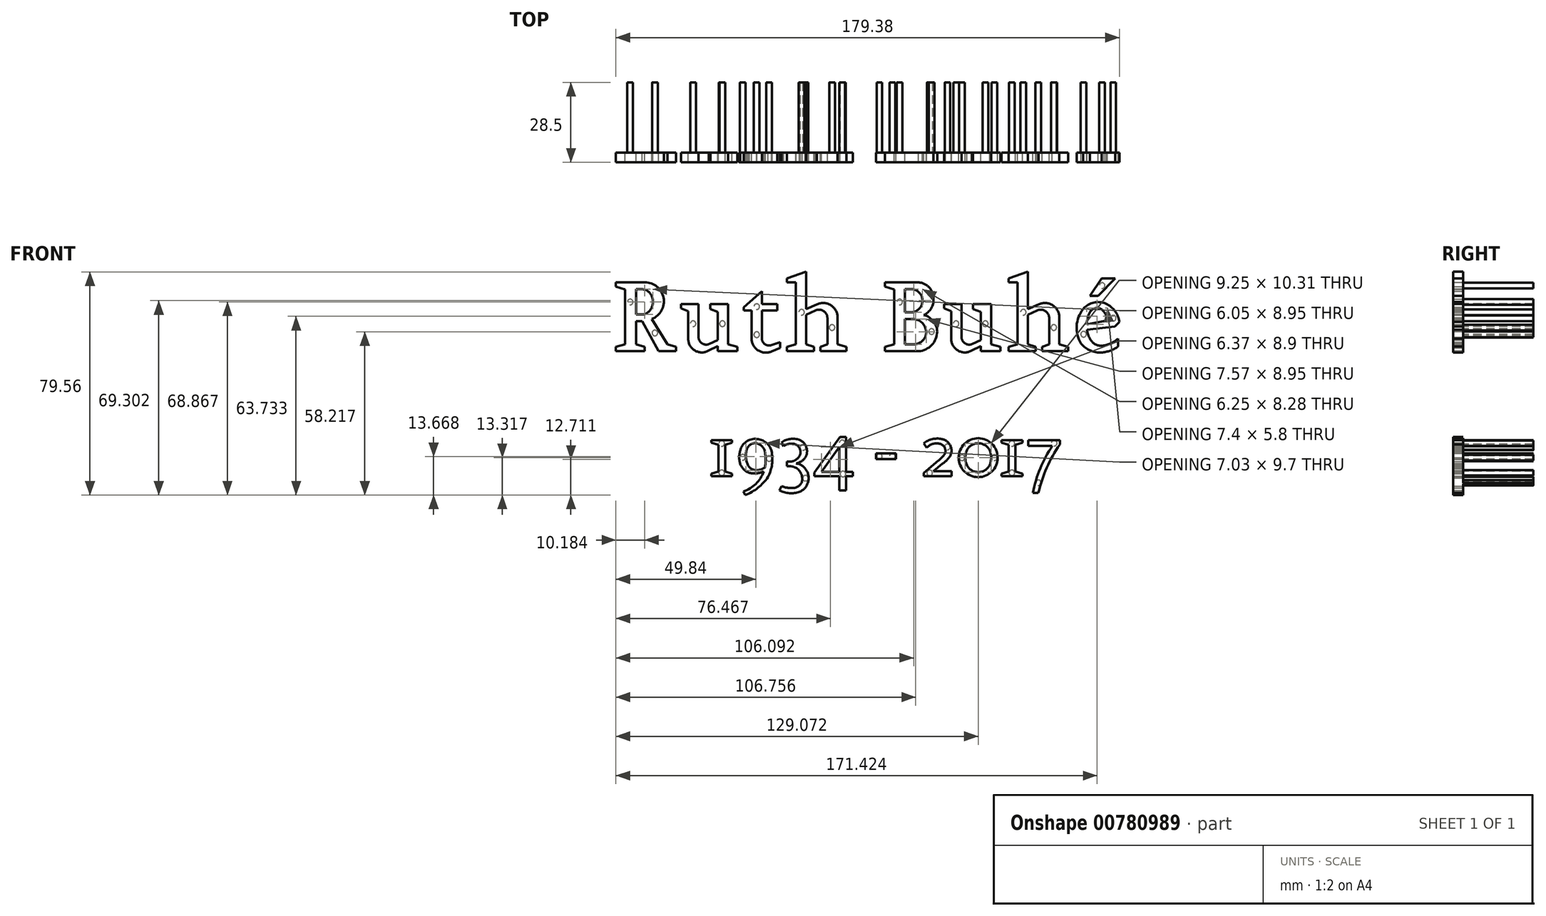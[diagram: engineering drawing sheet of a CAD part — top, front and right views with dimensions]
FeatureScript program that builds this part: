
annotation { "Feature Type Name" : "Feature", "Feature Type Description" : "" }
export const myFeature = defineFeature(function(context is Context, id is Id, definition is map)
    precondition{}
    {
        {
            var Q0;
            Q0=qCreatedBy(makeId("Front.planeOp"),FACE);
            var sketch = newSketch(context, id + "F0", { "sketchPlane" : qUnion([Q0])});
            skLineSegment(sketch, "E0", {"start": v(-78.02, 15.2) * mm, "end": v(-67.8, 15.2) * mm});
            skLineSegment(sketch, "E1", {"start": v(-67.8, 15.2) * mm, "end": v(-67.8, 16.73) * mm});
            skLineSegment(sketch, "E2", {"start": v(-67.8, 16.73) * mm, "end": v(-70.86, 17.67) * mm});
            skLineSegment(sketch, "E3", {"start": v(-70.86, 17.67) * mm, "end": v(-70.86, 25.9) * mm});
            skLineSegment(sketch, "E4", {"start": v(-70.86, 25.9) * mm, "end": v(-68.64, 25.9) * mm});
            skLineSegment(sketch, "E5", {"start": v(-68.64, 25.9) * mm, "end": v(-62.81, 15.2) * mm});
            skLineSegment(sketch, "E6", {"start": v(-62.81, 15.2) * mm, "end": v(-56.63, 15.2) * mm});
            skLineSegment(sketch, "E7", {"start": v(-56.63, 15.2) * mm, "end": v(-56.63, 16.73) * mm});
            skLineSegment(sketch, "E8", {"start": v(-56.63, 16.73) * mm, "end": v(-59.61, 17.67) * mm});
            skLineSegment(sketch, "E9", {"start": v(-59.61, 17.67) * mm, "end": v(-65.23, 26.62) * mm});
            skLineSegment(sketch, "E10", {"start": v(-78.02, 15.2) * mm, "end": v(-78.02, 16.73) * mm});
            skLineSegment(sketch, "E11", {"start": v(-78.02, 16.73) * mm, "end": v(-74.74, 17.67) * mm});
            skLineSegment(sketch, "E12", {"start": v(-74.74, 17.67) * mm, "end": v(-74.74, 37.23) * mm});
            skLineSegment(sketch, "E13", {"start": v(-74.74, 37.23) * mm, "end": v(-78.02, 38.21) * mm});
            skLineSegment(sketch, "E14", {"start": v(-78.02, 38.21) * mm, "end": v(-78.02, 39.74) * mm});
            skLineSegment(sketch, "E15", {"start": v(-78.02, 39.74) * mm, "end": v(-68.86, 39.74) * mm});
            skArc(sketch, "E16", {"start": v(-65.23, 26.62) * mm, "mid": v(-61.06, 34.23) * mm, "end": v(-67.76, 39.74) * mm});
            skArc(sketch, "E17", {"start": v(-67.74, 28.32) * mm, "mid": v(-64.81, 32.8) * mm, "end": v(-67.74, 37.27) * mm});
            skLineSegment(sketch, "E18", {"start": v(-67.74, 37.27) * mm, "end": v(-70.86, 37.27) * mm});
            skLineSegment(sketch, "E19", {"start": v(-70.86, 37.27) * mm, "end": v(-70.86, 28.32) * mm});
            skLineSegment(sketch, "E20", {"start": v(-70.86, 28.32) * mm, "end": v(-67.74, 28.32) * mm});
            skLineSegment(sketch, "E21", {"start": v(-68.86, 39.74) * mm, "end": v(-67.76, 39.74) * mm});
            skSolve(sketch);
        }
        {
            var Q0;
            Q0=makeQuery(id+"F0.imprint","IMPRINT",FACE,{"disambiguationData":[TD([[makeQuery(id+"F0.imprint","IMPRINT",EDGE,{"derivedFrom":sQuery(id+"F0.wireOp",EDGE,"E0")}),1.0]])]});
            extrude(context, id + "F1", {"entities" : qUnion([Q0]), "depth" : 3.5 * mm, "offsetDistance" : 25 * mm});
        }
        {
            var Q0;
            Q0=makeQuery(id+"F1.opExtrude","SWEPT_EDGE",EDGE,{"disambiguationData":[OSD([sQuery(id+"F0.wireOp",EDGE,"E17"),sQuery(id+"F0.wireOp",EDGE,"E18")])]});
            var Q1;
            Q1=makeQuery(id+"F1.opExtrude","SWEPT_EDGE",EDGE,{"disambiguationData":[OSD([sQuery(id+"F0.wireOp",EDGE,"E17"),sQuery(id+"F0.wireOp",EDGE,"E20")])]});
            fillet(context, id + "F2", {"entities" : qUnion([Q0, Q1]), "radius" : 3 * mm, "tangentPropagation" : true, "allowEdgeOverflow" : false});
        }
        {
            var Q0;
            Q0=qCreatedBy(makeId("Front.planeOp"),FACE);
            var sketch = newSketch(context, id + "F3", { "sketchPlane" : qUnion([Q0])});
            skLineSegment(sketch, "E22", {"start": v(-41.77, 15.2) * mm, "end": v(-34.7, 15.2) * mm});
            skLineSegment(sketch, "E23", {"start": v(-34.7, 15.2) * mm, "end": v(-34.7, 16.73) * mm});
            skLineSegment(sketch, "E24", {"start": v(-34.7, 16.73) * mm, "end": v(-38.08, 17.67) * mm});
            skLineSegment(sketch, "E25", {"start": v(-38.08, 17.67) * mm, "end": v(-38.08, 32) * mm});
            skLineSegment(sketch, "E26", {"start": v(-38.08, 32) * mm, "end": v(-44.47, 32) * mm});
            skLineSegment(sketch, "E27", {"start": v(-44.47, 32) * mm, "end": v(-44.47, 30.27) * mm});
            skLineSegment(sketch, "E28", {"start": v(-44.47, 30.27) * mm, "end": v(-41.77, 29.18) * mm});
            skLineSegment(sketch, "E29", {"start": v(-41.77, 29.18) * mm, "end": v(-41.77, 19.11) * mm});
            skLineSegment(sketch, "E30", {"start": v(-41.77, 15.2) * mm, "end": v(-41.77, 16.98) * mm});
            skLineSegment(sketch, "E31", {"start": v(-41.77, 16.98) * mm, "end": v(-45.17, 15.3) * mm});
            skLineSegment(sketch, "E32", {"start": v(-41.77, 19.11) * mm, "end": v(-44.76, 17.72) * mm});
            skLineSegment(sketch, "E33", {"start": v(-52.26, 19.48) * mm, "end": v(-52.26, 29.48) * mm});
            skLineSegment(sketch, "E34", {"start": v(-52.26, 29.48) * mm, "end": v(-54.82, 30.46) * mm});
            skLineSegment(sketch, "E35", {"start": v(-54.82, 30.46) * mm, "end": v(-54.82, 32) * mm});
            skLineSegment(sketch, "E36", {"start": v(-54.82, 32) * mm, "end": v(-48.6, 32) * mm});
            skLineSegment(sketch, "E37", {"start": v(-48.6, 32) * mm, "end": v(-48.6, 20.2) * mm});
            skArc(sketch, "E38", {"start": v(-52.26, 19.48) * mm, "mid": v(-49.87, 15.44) * mm, "end": v(-45.17, 15.3) * mm});
            skArc(sketch, "E39", {"start": v(-48.6, 20.2) * mm, "mid": v(-47.31, 17.98) * mm, "end": v(-44.76, 17.72) * mm});
            skSolve(sketch);
        }
        {
            var Q0;
            Q0=makeQuery(id+"F3.imprint","IMPRINT",FACE,{"disambiguationData":[TD([[makeQuery(id+"F3.imprint","IMPRINT",EDGE,{"derivedFrom":sQuery(id+"F3.wireOp",EDGE,"E22")}),1.0]])]});
            extrude(context, id + "F4", {"entities" : qUnion([Q0]), "depth" : 3.5 * mm, "offsetDistance" : 25 * mm});
        }
        {
            var Q0;
            Q0=qCreatedBy(makeId("Front.planeOp"),FACE);
            var sketch = newSketch(context, id + "F5", { "sketchPlane" : qUnion([Q0])});
            skLineSegment(sketch, "E40", {"start": v(-20.57, 32) * mm, "end": v(-26.02, 32) * mm});
            skLineSegment(sketch, "E41", {"start": v(-26.02, 32) * mm, "end": v(-26.02, 36.51) * mm});
            skLineSegment(sketch, "E42", {"start": v(-26.02, 36.51) * mm, "end": v(-32.46, 30.8) * mm});
            skLineSegment(sketch, "E43", {"start": v(-32.46, 30.8) * mm, "end": v(-32.46, 29.66) * mm});
            skLineSegment(sketch, "E44", {"start": v(-32.46, 29.66) * mm, "end": v(-29.69, 29.66) * mm});
            skLineSegment(sketch, "E45", {"start": v(-29.69, 29.66) * mm, "end": v(-29.69, 19.66) * mm});
            skLineSegment(sketch, "E46", {"start": v(-20.57, 32) * mm, "end": v(-20.57, 29.66) * mm});
            skLineSegment(sketch, "E47", {"start": v(-20.57, 29.66) * mm, "end": v(-26.02, 29.66) * mm});
            skLineSegment(sketch, "E48", {"start": v(-26.02, 29.66) * mm, "end": v(-26.02, 19.66) * mm});
            skLineSegment(sketch, "E49", {"start": v(-22.55, 17.37) * mm, "end": v(-19.53, 18.45) * mm});
            skLineSegment(sketch, "E50", {"start": v(-19.53, 18.45) * mm, "end": v(-19.53, 16.4) * mm});
            skLineSegment(sketch, "E51", {"start": v(-19.53, 16.4) * mm, "end": v(-22.56, 15.09) * mm});
            skArc(sketch, "E52", {"start": v(-29.69, 19.66) * mm, "mid": v(-27.34, 15.48) * mm, "end": v(-22.56, 15.09) * mm});
            skArc(sketch, "E53", {"start": v(-26.02, 19.66) * mm, "mid": v(-24.85, 17.65) * mm, "end": v(-22.55, 17.37) * mm});
            skSolve(sketch);
        }
        {
            var Q0;
            Q0=makeQuery(id+"F5.imprint","IMPRINT",FACE,{"disambiguationData":[TD([[makeQuery(id+"F5.imprint","IMPRINT",EDGE,{"derivedFrom":sQuery(id+"F5.wireOp",EDGE,"E40")}),1.0]])]});
            extrude(context, id + "F6", {"entities" : qUnion([Q0]), "depth" : 3.5 * mm, "offsetDistance" : 25 * mm});
        }
        {
            var Q0;
            Q0=qCreatedBy(makeId("Front.planeOp"),FACE);
            var sketch = newSketch(context, id + "F7", { "sketchPlane" : qUnion([Q0])});
            skLineSegment(sketch, "E54", {"start": v(-17.06, 15.2) * mm, "end": v(-7.42, 15.2) * mm});
            skLineSegment(sketch, "E55", {"start": v(-7.42, 15.2) * mm, "end": v(-7.42, 16.73) * mm});
            skLineSegment(sketch, "E56", {"start": v(-7.42, 16.73) * mm, "end": v(-10.26, 17.67) * mm});
            skLineSegment(sketch, "E57", {"start": v(-10.26, 17.67) * mm, "end": v(-10.26, 28.2) * mm});
            skLineSegment(sketch, "E58", {"start": v(-10.26, 28.2) * mm, "end": v(-6.9, 29.76) * mm});
            skLineSegment(sketch, "E59", {"start": v(-17.06, 15.2) * mm, "end": v(-17.06, 16.73) * mm});
            skLineSegment(sketch, "E60", {"start": v(-17.06, 16.73) * mm, "end": v(-13.88, 17.67) * mm});
            skLineSegment(sketch, "E61", {"start": v(-13.88, 17.67) * mm, "end": v(-13.88, 39.74) * mm});
            skLineSegment(sketch, "E62", {"start": v(-13.88, 39.74) * mm, "end": v(-17.06, 39.74) * mm});
            skLineSegment(sketch, "E63", {"start": v(-17.06, 39.74) * mm, "end": v(-17.06, 41.1) * mm});
            skLineSegment(sketch, "E64", {"start": v(-17.06, 41.1) * mm, "end": v(-10.26, 43.5) * mm});
            skLineSegment(sketch, "E65", {"start": v(-10.26, 43.5) * mm, "end": v(-10.26, 30.24) * mm});
            skLineSegment(sketch, "E66", {"start": v(-10.26, 30.24) * mm, "end": v(-6.4, 31.9) * mm});
            skLineSegment(sketch, "E67", {"start": v(-2.67, 27.17) * mm, "end": v(-2.67, 17.67) * mm});
            skLineSegment(sketch, "E68", {"start": v(-2.67, 17.67) * mm, "end": v(-5.22, 16.73) * mm});
            skLineSegment(sketch, "E69", {"start": v(-5.22, 16.73) * mm, "end": v(-5.22, 15.2) * mm});
            skLineSegment(sketch, "E70", {"start": v(-5.22, 15.2) * mm, "end": v(4.1, 15.2) * mm});
            skLineSegment(sketch, "E71", {"start": v(4.1, 15.2) * mm, "end": v(4.1, 16.73) * mm});
            skLineSegment(sketch, "E72", {"start": v(4.1, 16.73) * mm, "end": v(0.99, 17.67) * mm});
            skLineSegment(sketch, "E73", {"start": v(0.99, 17.67) * mm, "end": v(0.99, 27.07) * mm});
            skArc(sketch, "E74", {"start": v(0.99, 27.07) * mm, "mid": v(-1.37, 31.53) * mm, "end": v(-6.4, 31.9) * mm});
            skArc(sketch, "E75", {"start": v(-2.67, 27.17) * mm, "mid": v(-4.12, 29.56) * mm, "end": v(-6.9, 29.76) * mm});
            skSolve(sketch);
        }
        {
            var Q0;
            Q0=makeQuery(id+"F7.imprint","IMPRINT",FACE,{"disambiguationData":[TD([[makeQuery(id+"F7.imprint","IMPRINT",EDGE,{"derivedFrom":sQuery(id+"F7.wireOp",EDGE,"E54")}),1.0]])]});
            extrude(context, id + "F8", {"entities" : qUnion([Q0]), "depth" : 3.5 * mm, "offsetDistance" : 25 * mm});
        }
        {
            var Q0;
            Q0=qCreatedBy(makeId("Front.planeOp"),FACE);
            var sketch = newSketch(context, id + "F9", { "sketchPlane" : qUnion([Q0])});
            skLineSegment(sketch, "E76", {"start": v(29.79, 15.2) * mm, "end": v(17.79, 15.2) * mm});
            skLineSegment(sketch, "E77", {"start": v(17.79, 15.2) * mm, "end": v(17.79, 16.73) * mm});
            skLineSegment(sketch, "E78", {"start": v(17.79, 16.73) * mm, "end": v(21.07, 17.67) * mm});
            skLineSegment(sketch, "E79", {"start": v(21.07, 17.67) * mm, "end": v(21.07, 37.23) * mm});
            skLineSegment(sketch, "E80", {"start": v(21.07, 37.23) * mm, "end": v(17.79, 38.21) * mm});
            skLineSegment(sketch, "E81", {"start": v(17.79, 38.21) * mm, "end": v(17.79, 39.74) * mm});
            skLineSegment(sketch, "E82", {"start": v(17.79, 39.74) * mm, "end": v(29.42, 39.74) * mm});
            skLineSegment(sketch, "E83", {"start": v(27.65, 37.37) * mm, "end": v(24.95, 37.37) * mm});
            skLineSegment(sketch, "E84", {"start": v(24.95, 37.37) * mm, "end": v(24.95, 29.1) * mm});
            skLineSegment(sketch, "E85", {"start": v(24.95, 29.1) * mm, "end": v(27.65, 29.1) * mm});
            skLineSegment(sketch, "E86", {"start": v(27.84, 26.62) * mm, "end": v(24.95, 26.62) * mm});
            skLineSegment(sketch, "E87", {"start": v(24.95, 26.62) * mm, "end": v(24.95, 17.67) * mm});
            skLineSegment(sketch, "E88", {"start": v(24.95, 17.67) * mm, "end": v(28.14, 17.67) * mm});
            skArc(sketch, "E89", {"start": v(35.13, 33.82) * mm, "mid": v(33.53, 38) * mm, "end": v(29.42, 39.74) * mm});
            skArc(sketch, "E90", {"start": v(31.72, 28.11) * mm, "mid": v(34.29, 30.45) * mm, "end": v(35.13, 33.82) * mm});
            skArc(sketch, "E91", {"start": v(36.45, 22.2) * mm, "mid": v(35.03, 25.92) * mm, "end": v(31.72, 28.11) * mm});
            skArc(sketch, "E92", {"start": v(29.79, 15.2) * mm, "mid": v(34.49, 17.4) * mm, "end": v(36.45, 22.2) * mm});
            skArc(sketch, "E93", {"start": v(32.52, 22.31) * mm, "mid": v(31.02, 25.38) * mm, "end": v(27.84, 26.62) * mm});
            skArc(sketch, "E94", {"start": v(28.14, 17.67) * mm, "mid": v(31.33, 19.05) * mm, "end": v(32.52, 22.31) * mm});
            skArc(sketch, "E95", {"start": v(27.65, 29.1) * mm, "mid": v(31.2, 33.23) * mm, "end": v(27.65, 37.37) * mm});
            skSolve(sketch);
        }
        {
            var Q0;
            Q0=makeQuery(id+"F9.imprint","IMPRINT",FACE,{"disambiguationData":[TD([[makeQuery(id+"F9.imprint","IMPRINT",EDGE,{"derivedFrom":sQuery(id+"F9.wireOp",EDGE,"E76")}),-1.0]])]});
            extrude(context, id + "F10", {"entities" : qUnion([Q0]), "depth" : 3.5 * mm, "offsetDistance" : 25 * mm});
        }
        {
            var Q0;
            Q0=makeQuery(id+"F10.opExtrude","SWEPT_EDGE",EDGE,{"disambiguationData":[OSD([sQuery(id+"F9.wireOp",EDGE,"E83"),sQuery(id+"F9.wireOp",EDGE,"E95")])]});
            var Q1;
            Q1=makeQuery(id+"F10.opExtrude","SWEPT_EDGE",EDGE,{"disambiguationData":[OSD([sQuery(id+"F9.wireOp",EDGE,"E85"),sQuery(id+"F9.wireOp",EDGE,"E95")])]});
            fillet(context, id + "F11", {"entities" : qUnion([Q0, Q1]), "radius" : 3 * mm, "tangentPropagation" : true, "allowEdgeOverflow" : false});
        }
        {
            var Q0;
            Q0=qCreatedBy(makeId("Front.planeOp"),FACE);
            var sketch = newSketch(context, id + "F12", { "sketchPlane" : qUnion([Q0])});
            skLineSegment(sketch, "E96", {"start": v(90.8, 34.88) * mm, "end": v(93.74, 34.88) * mm});
            skLineSegment(sketch, "E97", {"start": v(93.74, 34.88) * mm, "end": v(99.81, 41.18) * mm});
            skLineSegment(sketch, "E98", {"start": v(99.81, 41.18) * mm, "end": v(95.06, 41.18) * mm});
            skLineSegment(sketch, "E99", {"start": v(95.06, 41.18) * mm, "end": v(90.8, 34.88) * mm});
            skLineSegment(sketch, "E100", {"start": v(99.7, 23.95) * mm, "end": v(101.36, 25.66) * mm});
            skArc(sketch, "E101", {"start": v(101.36, 25.66) * mm, "mid": v(99.76, 29.5) * mm, "end": v(96.55, 32.12) * mm});
            skArc(sketch, "E102", {"start": v(96.55, 32.12) * mm, "mid": v(92.2, 32.52) * mm, "end": v(88.49, 30.24) * mm});
            skArc(sketch, "E103", {"start": v(88.49, 30.24) * mm, "mid": v(86.13, 24.18) * mm, "end": v(87.72, 17.87) * mm});
            skArc(sketch, "E104", {"start": v(87.72, 17.87) * mm, "mid": v(91.03, 15.46) * mm, "end": v(95.06, 14.72) * mm});
            skArc(sketch, "E105", {"start": v(95.06, 14.72) * mm, "mid": v(98.1, 15.4) * mm, "end": v(100.86, 16.82) * mm});
            skLineSegment(sketch, "E106", {"start": v(100.86, 16.82) * mm, "end": v(100.86, 19.7) * mm});
            skArc(sketch, "E107", {"start": v(94.95, 17.1) * mm, "mid": v(98.11, 17.92) * mm, "end": v(100.86, 19.7) * mm});
            skArc(sketch, "E108", {"start": v(90.8, 19.7) * mm, "mid": v(92.53, 17.83) * mm, "end": v(94.95, 17.1) * mm});
            skArc(sketch, "E109", {"start": v(90.8, 29.14) * mm, "mid": v(89.98, 26.84) * mm, "end": v(89.7, 24.42) * mm});
            skArc(sketch, "E110", {"start": v(95.94, 29.14) * mm, "mid": v(93.38, 30.56) * mm, "end": v(90.8, 29.14) * mm});
            skArc(sketch, "E111", {"start": v(97.1, 26.21) * mm, "mid": v(96.68, 27.74) * mm, "end": v(95.94, 29.14) * mm});
            skLineSegment(sketch, "E112", {"start": v(99.7, 23.95) * mm, "end": v(89.81, 22.85) * mm});
            skLineSegment(sketch, "E113", {"start": v(97.1, 26.21) * mm, "end": v(89.7, 24.76) * mm});
            skPoint(sketch, "E113.endSnap0", {"position": v(89.7, 24.42) * mm});
            skArc(sketch, "E114.trimOffspring", {"start": v(89.81, 22.85) * mm, "mid": v(90.19, 21.23) * mm, "end": v(90.8, 19.7) * mm});
            skPoint(sketch, "E115.orphan", {"position": v(87.94, 24.42) * mm});
            skSolve(sketch);
        }
        {
            var Q0;
            Q0=makeQuery(id+"F12.imprint","IMPRINT",FACE,{"disambiguationData":[TD([[makeQuery(id+"F12.imprint","IMPRINT",EDGE,{"derivedFrom":sQuery(id+"F12.wireOp",EDGE,"E100")}),1.0]])]});
            var Q1;
            Q1=makeQuery(id+"F12.imprint","IMPRINT",FACE,{"disambiguationData":[TD([[makeQuery(id+"F12.imprint","IMPRINT",EDGE,{"derivedFrom":sQuery(id+"F12.wireOp",EDGE,"E96")}),1.0]])]});
            extrude(context, id + "F13", {"entities" : qUnion([Q0, Q1]), "depth" : 3.5 * mm, "offsetDistance" : 25 * mm});
        }
        {
            var Q0;
            Q0=makeQuery(id+"F4.opExtrude","SWEPT_BODY",BODY,{"disambiguationData":[OSD([sQuery(id+"F3.wireOp",EDGE,"E22"),sQuery(id+"F3.wireOp",EDGE,"E23"),sQuery(id+"F3.wireOp",EDGE,"E24"),sQuery(id+"F3.wireOp",EDGE,"E25"),sQuery(id+"F3.wireOp",EDGE,"E26"),sQuery(id+"F3.wireOp",EDGE,"E27"),sQuery(id+"F3.wireOp",EDGE,"E28"),sQuery(id+"F3.wireOp",EDGE,"E29"),sQuery(id+"F3.wireOp",EDGE,"E30"),sQuery(id+"F3.wireOp",EDGE,"E31"),sQuery(id+"F3.wireOp",EDGE,"E32"),sQuery(id+"F3.wireOp",EDGE,"E33"),sQuery(id+"F3.wireOp",EDGE,"E34"),sQuery(id+"F3.wireOp",EDGE,"E35"),sQuery(id+"F3.wireOp",EDGE,"E36"),sQuery(id+"F3.wireOp",EDGE,"E37"),sQuery(id+"F3.wireOp",EDGE,"E38"),sQuery(id+"F3.wireOp",EDGE,"E39")])]});
            transform(context, id + "F14", {"entities" : qUnion([Q0]), "transformType" : TransformType.TRANSLATION_3D, "dx" : 94.3 * mm, "dy" : 0 * mm, "dz" : 0 * mm, "makeCopy" : true});
        }
        {
            var Q0;
            Q0=makeQuery(id+"F8.opExtrude","SWEPT_BODY",BODY,{"disambiguationData":[OSD([sQuery(id+"F7.wireOp",EDGE,"E54"),sQuery(id+"F7.wireOp",EDGE,"E55"),sQuery(id+"F7.wireOp",EDGE,"E56"),sQuery(id+"F7.wireOp",EDGE,"E57"),sQuery(id+"F7.wireOp",EDGE,"E58"),sQuery(id+"F7.wireOp",EDGE,"E59"),sQuery(id+"F7.wireOp",EDGE,"E60"),sQuery(id+"F7.wireOp",EDGE,"E61"),sQuery(id+"F7.wireOp",EDGE,"E62"),sQuery(id+"F7.wireOp",EDGE,"E63"),sQuery(id+"F7.wireOp",EDGE,"E64"),sQuery(id+"F7.wireOp",EDGE,"E65"),sQuery(id+"F7.wireOp",EDGE,"E66"),sQuery(id+"F7.wireOp",EDGE,"E67"),sQuery(id+"F7.wireOp",EDGE,"E68"),sQuery(id+"F7.wireOp",EDGE,"E69"),sQuery(id+"F7.wireOp",EDGE,"E70"),sQuery(id+"F7.wireOp",EDGE,"E71"),sQuery(id+"F7.wireOp",EDGE,"E72"),sQuery(id+"F7.wireOp",EDGE,"E73"),sQuery(id+"F7.wireOp",EDGE,"E74"),sQuery(id+"F7.wireOp",EDGE,"E75")])]});
            transform(context, id + "F15", {"entities" : qUnion([Q0]), "transformType" : TransformType.TRANSLATION_3D, "dx" : 79.7 * mm, "dy" : 0 * mm, "dz" : 0 * mm, "makeCopy" : true});
        }
        {
            var Q0;
            Q0=qCreatedBy(makeId("Front.planeOp"),FACE);
            var sketch = newSketch(context, id + "F16", { "sketchPlane" : qUnion([Q0])});
            skLineSegment(sketch, "E116", {"start": v(-44.04, -29.35) * mm, "end": v(-36.6, -29.35) * mm});
            skLineSegment(sketch, "E117", {"start": v(-36.6, -29.35) * mm, "end": v(-36.6, -28.47) * mm});
            skLineSegment(sketch, "E118", {"start": v(-36.6, -28.47) * mm, "end": v(-39.1, -27.72) * mm});
            skLineSegment(sketch, "E119", {"start": v(-39.1, -27.72) * mm, "end": v(-39.1, -18.13) * mm});
            skLineSegment(sketch, "E120", {"start": v(-39.1, -18.13) * mm, "end": v(-36.6, -17.38) * mm});
            skLineSegment(sketch, "E121", {"start": v(-36.6, -17.38) * mm, "end": v(-36.6, -16.5) * mm});
            skLineSegment(sketch, "E122", {"start": v(-36.6, -16.5) * mm, "end": v(-44.04, -16.5) * mm});
            skLineSegment(sketch, "E123", {"start": v(-44.04, -16.5) * mm, "end": v(-44.04, -17.38) * mm});
            skLineSegment(sketch, "E124", {"start": v(-44.04, -17.38) * mm, "end": v(-41.53, -18.13) * mm});
            skLineSegment(sketch, "E125", {"start": v(-41.53, -18.13) * mm, "end": v(-41.53, -27.72) * mm});
            skLineSegment(sketch, "E126", {"start": v(-41.53, -27.72) * mm, "end": v(-44.04, -28.47) * mm});
            skLineSegment(sketch, "E127", {"start": v(-44.04, -28.47) * mm, "end": v(-44.04, -29.35) * mm});
            skSolve(sketch);
        }
        {
            var Q0;
            Q0=makeQuery(id+"F16.imprint","IMPRINT",FACE,{"disambiguationData":[TD([[makeQuery(id+"F16.imprint","IMPRINT",EDGE,{"derivedFrom":sQuery(id+"F16.wireOp",EDGE,"E116")}),1.0]])]});
            extrude(context, id + "F17", {"entities" : qUnion([Q0]), "depth" : 3.5 * mm, "offsetDistance" : 25 * mm});
        }
        {
            var Q0;
            Q0=makeQuery(id+"F17.opExtrude","SWEPT_BODY",BODY,{"disambiguationData":[OSD([sQuery(id+"F16.wireOp",EDGE,"E116"),sQuery(id+"F16.wireOp",EDGE,"E117"),sQuery(id+"F16.wireOp",EDGE,"E118"),sQuery(id+"F16.wireOp",EDGE,"E119"),sQuery(id+"F16.wireOp",EDGE,"E120"),sQuery(id+"F16.wireOp",EDGE,"E121"),sQuery(id+"F16.wireOp",EDGE,"E122"),sQuery(id+"F16.wireOp",EDGE,"E123"),sQuery(id+"F16.wireOp",EDGE,"E124"),sQuery(id+"F16.wireOp",EDGE,"E125"),sQuery(id+"F16.wireOp",EDGE,"E126"),sQuery(id+"F16.wireOp",EDGE,"E127")])]});
            transform(context, id + "F18", {"entities" : qUnion([Q0]), "transformType" : TransformType.TRANSLATION_3D, "dx" : 104.3 * mm, "dy" : 0 * mm, "dz" : 0 * mm, "makeCopy" : true});
        }
        {
            var Q0;
            Q0=qCreatedBy(makeId("Front.planeOp"),FACE);
            var sketch = newSketch(context, id + "F19", { "sketchPlane" : qUnion([Q0])});
            skLineSegment(sketch, "E128", {"start": v(3.98, -15.35) * mm, "end": v(3.98, -27.8) * mm});
            skLineSegment(sketch, "E129", {"start": v(3.98, -34.4) * mm, "end": v(1.63, -34.4) * mm});
            skLineSegment(sketch, "E130", {"start": v(1.63, -34.4) * mm, "end": v(1.63, -29.38) * mm});
            skLineSegment(sketch, "E131", {"start": v(1.63, -18.9) * mm, "end": v(-4.74, -27.8) * mm});
            skLineSegment(sketch, "E132", {"start": v(-4.74, -27.8) * mm, "end": v(1.63, -27.8) * mm});
            skLineSegment(sketch, "E133", {"start": v(6.36, -27.8) * mm, "end": v(6.36, -29.38) * mm});
            skLineSegment(sketch, "E134", {"start": v(6.36, -29.38) * mm, "end": v(3.98, -29.38) * mm});
            skLineSegment(sketch, "E135", {"start": v(-7.27, -29.38) * mm, "end": v(-7.27, -28.07) * mm});
            skLineSegment(sketch, "E136", {"start": v(-7.27, -28.07) * mm, "end": v(1.83, -15.35) * mm});
            skLineSegment(sketch, "E137", {"start": v(1.83, -15.35) * mm, "end": v(3.98, -15.35) * mm});
            skLineSegment(sketch, "E138.trimOffspring", {"start": v(3.98, -27.8) * mm, "end": v(6.36, -27.8) * mm});
            skLineSegment(sketch, "E139.trimOffspring", {"start": v(1.63, -29.38) * mm, "end": v(-7.27, -29.38) * mm});
            skLineSegment(sketch, "E140.trimOffspring", {"start": v(1.63, -27.8) * mm, "end": v(1.63, -18.9) * mm});
            skLineSegment(sketch, "E141.trimOffspring", {"start": v(3.98, -29.38) * mm, "end": v(3.98, -34.4) * mm});
            skSolve(sketch);
        }
        {
            var Q0;
            Q0=makeQuery(id+"F19.imprint","IMPRINT",FACE,{"disambiguationData":[TD([[makeQuery(id+"F19.imprint","IMPRINT",EDGE,{"derivedFrom":sQuery(id+"F19.wireOp",EDGE,"E128")}),-1.0]])]});
            extrude(context, id + "F20", {"entities" : qUnion([Q0]), "depth" : 3.5 * mm, "offsetDistance" : 25 * mm});
        }
        {
            var Q0;
            Q0=qCreatedBy(makeId("Front.planeOp"),FACE);
            var sketch = newSketch(context, id + "F21", { "sketchPlane" : qUnion([Q0])});
            skLineSegment(sketch, "E142", {"start": v(77.45, -18.55) * mm, "end": v(68.9, -18.55) * mm});
            skLineSegment(sketch, "E143", {"start": v(68.9, -18.55) * mm, "end": v(68.9, -16.5) * mm});
            skLineSegment(sketch, "E144", {"start": v(68.9, -16.5) * mm, "end": v(80.12, -16.5) * mm});
            skLineSegment(sketch, "E145", {"start": v(80.12, -16.5) * mm, "end": v(80.12, -18.07) * mm});
            skLineSegment(sketch, "E146", {"start": v(70.5, -35.3) * mm, "end": v(72.5, -35.3) * mm});
            skArc(sketch, "E147", {"start": v(77.45, -18.55) * mm, "mid": v(73.16, -26.58) * mm, "end": v(70.5, -35.3) * mm});
            skArc(sketch, "E148", {"start": v(80.12, -18.07) * mm, "mid": v(75.5, -26.32) * mm, "end": v(72.5, -35.3) * mm});
            skSolve(sketch);
        }
        {
            var Q0;
            Q0=makeQuery(id+"F21.imprint","IMPRINT",FACE,{"disambiguationData":[TD([[makeQuery(id+"F21.imprint","IMPRINT",EDGE,{"derivedFrom":sQuery(id+"F21.wireOp",EDGE,"E142")}),-1.0]])]});
            extrude(context, id + "F22", {"entities" : qUnion([Q0]), "depth" : 3.5 * mm, "offsetDistance" : 25 * mm});
        }
        {
            var Q0;
            Q0=qCreatedBy(makeId("Front.planeOp"),FACE);
            var sketch = newSketch(context, id + "F23", { "sketchPlane" : qUnion([Q0])});
            skCircle(sketch, "E149", {"center": v(51.05, -22.75) * mm, "radius": 6.94 * mm});
            skPoint(sketch, "E149.first.point", {"position": v(51, -15.8) * mm});
            skPoint(sketch, "E149.second.point", {"position": v(45.69, -27.17) * mm});
            skPoint(sketch, "E149.third.point", {"position": v(55.6, -28) * mm});
            skArc(sketch, "E150", {"start": v(55.13, -20.1) * mm, "mid": v(51.07, -17.6) * mm, "end": v(47, -20.1) * mm});
            skArc(sketch, "E151", {"start": v(55.13, -25.4) * mm, "mid": v(55.68, -22.75) * mm, "end": v(55.13, -20.1) * mm});
            skArc(sketch, "E152", {"start": v(47, -25.4) * mm, "mid": v(51.07, -27.9) * mm, "end": v(55.13, -25.4) * mm});
            skArc(sketch, "E153", {"start": v(47, -20.1) * mm, "mid": v(46.43, -22.75) * mm, "end": v(47, -25.4) * mm});
            skSolve(sketch);
        }
        {
            var Q0;
            Q0=makeQuery(id+"F23.imprint","IMPRINT",FACE,{"disambiguationData":[TD([[makeQuery(id+"F23.imprint","IMPRINT",EDGE,{"derivedFrom":sQuery(id+"F23.wireOp",EDGE,"E149")}),1.0]])]});
            extrude(context, id + "F24", {"entities" : qUnion([Q0]), "depth" : 3.5 * mm, "offsetDistance" : 25 * mm});
        }
        {
            var Q0;
            Q0=qCreatedBy(makeId("Front.planeOp"),FACE);
            var sketch = newSketch(context, id + "F25", { "sketchPlane" : qUnion([Q0])});
            skLineSegment(sketch, "E154", {"start": v(-32.6, -34.83) * mm, "end": v(-31.92, -36.07) * mm});
            skArc(sketch, "E155", {"start": v(-31.92, -36.07) * mm, "mid": v(-27.4, -33.47) * mm, "end": v(-23.88, -29.64) * mm});
            skArc(sketch, "E156", {"start": v(-23.88, -29.64) * mm, "mid": v(-22.4, -25.11) * mm, "end": v(-22.58, -20.35) * mm});
            skArc(sketch, "E157", {"start": v(-22.58, -20.35) * mm, "mid": v(-24.48, -17.39) * mm, "end": v(-27.75, -16.08) * mm});
            skArc(sketch, "E158", {"start": v(-27.75, -16.08) * mm, "mid": v(-31.59, -17.06) * mm, "end": v(-33.8, -20.35) * mm});
            skArc(sketch, "E159", {"start": v(-33.8, -20.35) * mm, "mid": v(-34.09, -22.6) * mm, "end": v(-33.8, -24.86) * mm});
            skArc(sketch, "E160", {"start": v(-33.8, -24.86) * mm, "mid": v(-32.49, -26.9) * mm, "end": v(-30.42, -28.18) * mm});
            skArc(sketch, "E161", {"start": v(-30.42, -28.18) * mm, "mid": v(-27.86, -28.35) * mm, "end": v(-25.36, -27.73) * mm});
            skArc(sketch, "E162", {"start": v(-32.6, -34.83) * mm, "mid": v(-28.19, -32.08) * mm, "end": v(-25.36, -27.73) * mm});
            skArc(sketch, "E163", {"start": v(-24.9, -26.21) * mm, "mid": v(-24.66, -23.55) * mm, "end": v(-24.9, -20.88) * mm});
            skArc(sketch, "E164", {"start": v(-24.9, -20.88) * mm, "mid": v(-25.91, -18.76) * mm, "end": v(-27.94, -17.58) * mm});
            skPoint(sketch, "E165", {"position": v(-34.09, -22.6) * mm});
            skPoint(sketch, "E166", {"position": v(-31.68, -22.64) * mm});
            skArc(sketch, "E167", {"start": v(-27.94, -17.58) * mm, "mid": v(-30, -18) * mm, "end": v(-31.34, -19.63) * mm});
            skArc(sketch, "E168", {"start": v(-31.34, -19.63) * mm, "mid": v(-31.68, -22.61) * mm, "end": v(-30.95, -25.53) * mm});
            skArc(sketch, "E169", {"start": v(-30.95, -25.53) * mm, "mid": v(-29.66, -26.77) * mm, "end": v(-27.94, -27.25) * mm});
            skArc(sketch, "E170", {"start": v(-27.94, -27.25) * mm, "mid": v(-26.37, -26.95) * mm, "end": v(-24.92, -26.27) * mm});
            skArc(sketch, "E171.trimOffspring", {"start": v(-24.92, -26.27) * mm, "mid": v(-24.91, -26.24) * mm, "end": v(-24.9, -26.21) * mm});
            skPoint(sketch, "E172.orphan", {"position": v(-23.96, -25.53) * mm});
            skSolve(sketch);
        }
        {
            var Q0;
            Q0=makeQuery(id+"F25.imprint","IMPRINT",FACE,{"disambiguationData":[TD([[makeQuery(id+"F25.imprint","IMPRINT",EDGE,{"derivedFrom":sQuery(id+"F25.wireOp",EDGE,"E154")}),1.0]])]});
            extrude(context, id + "F26", {"entities" : qUnion([Q0]), "depth" : 3.5 * mm, "offsetDistance" : 25 * mm});
        }
        {
            var Q0;
            Q0=qCreatedBy(makeId("Front.planeOp"),FACE);
            var sketch = newSketch(context, id + "F27", { "sketchPlane" : qUnion([Q0])});
            skLineSegment(sketch, "E173", {"start": v(-19.06, -17.35) * mm, "end": v(-18.22, -18.65) * mm});
            skLineSegment(sketch, "E174", {"start": v(-17.14, -24.16) * mm, "end": v(-17.14, -25.79) * mm});
            skLineSegment(sketch, "E175", {"start": v(-19.06, -32.87) * mm, "end": v(-19.75, -34.37) * mm});
            skArc(sketch, "E176", {"start": v(-12.61, -16.41) * mm, "mid": v(-15.95, -16.09) * mm, "end": v(-19.06, -17.35) * mm});
            skArc(sketch, "E177", {"start": v(-10.6, -22.78) * mm, "mid": v(-10.12, -19.12) * mm, "end": v(-12.61, -16.41) * mm});
            skArc(sketch, "E178", {"start": v(-13.75, -24.8) * mm, "mid": v(-11.98, -24.08) * mm, "end": v(-10.6, -22.78) * mm});
            skArc(sketch, "E179", {"start": v(-19.75, -34.37) * mm, "mid": v(-16.24, -35.41) * mm, "end": v(-12.61, -34.9) * mm});
            skArc(sketch, "E180", {"start": v(-12.61, -34.9) * mm, "mid": v(-9.5, -31.3) * mm, "end": v(-10.6, -26.67) * mm});
            skArc(sketch, "E181", {"start": v(-10.6, -26.67) * mm, "mid": v(-12, -25.43) * mm, "end": v(-13.75, -24.8) * mm});
            skArc(sketch, "E182", {"start": v(-13.75, -18.1) * mm, "mid": v(-16.05, -17.8) * mm, "end": v(-18.22, -18.65) * mm});
            skArc(sketch, "E183", {"start": v(-13.75, -23.42) * mm, "mid": v(-12.26, -20.76) * mm, "end": v(-13.75, -18.1) * mm});
            skLineSegment(sketch, "E184", {"start": v(-17.14, -24.16) * mm, "end": v(-16.1, -24.16) * mm});
            skLineSegment(sketch, "E185", {"start": v(-17.14, -25.79) * mm, "end": v(-16.1, -25.79) * mm});
            skArc(sketch, "E186", {"start": v(-16.1, -24.16) * mm, "mid": v(-14.87, -23.97) * mm, "end": v(-13.75, -23.42) * mm});
            skArc(sketch, "E187", {"start": v(-11.68, -29.94) * mm, "mid": v(-13.07, -26.99) * mm, "end": v(-16.1, -25.79) * mm});
            skArc(sketch, "E188", {"start": v(-19.06, -32.87) * mm, "mid": v(-16.72, -33.52) * mm, "end": v(-14.29, -33.48) * mm});
            skArc(sketch, "E189", {"start": v(-14.29, -33.48) * mm, "mid": v(-12.26, -32.25) * mm, "end": v(-11.68, -29.94) * mm});
            skSolve(sketch);
        }
        {
            var Q0;
            Q0=makeQuery(id+"F27.imprint","IMPRINT",FACE,{"disambiguationData":[TD([[makeQuery(id+"F27.imprint","IMPRINT",EDGE,{"derivedFrom":sQuery(id+"F27.wireOp",EDGE,"E173")}),1.0]])]});
            extrude(context, id + "F28", {"entities" : qUnion([Q0]), "depth" : 3.5 * mm, "offsetDistance" : 25 * mm});
        }
        {
            var Q0;
            Q0=qCreatedBy(makeId("Front.planeOp"),FACE);
            var sketch = newSketch(context, id + "F29", { "sketchPlane" : qUnion([Q0])});
            skLineSegment(sketch, "E190.bottom", {"start": v(14.61, -21.22) * mm, "end": v(21.72, -21.22) * mm});
            skLineSegment(sketch, "E190.top", {"start": v(14.61, -23.3) * mm, "end": v(21.72, -23.3) * mm});
            skLineSegment(sketch, "E190.left", {"start": v(14.61, -21.22) * mm, "end": v(14.61, -23.3) * mm});
            skLineSegment(sketch, "E190.right", {"start": v(21.72, -21.22) * mm, "end": v(21.72, -23.3) * mm});
            skSolve(sketch);
        }
        {
            var Q0;
            Q0=makeQuery(id+"F29.imprint","IMPRINT",FACE,{"disambiguationData":[TD([[makeQuery(id+"F29.imprint","IMPRINT",EDGE,{"derivedFrom":sQuery(id+"F29.wireOp",EDGE,"E190.bottom")}),-1.0]])]});
            extrude(context, id + "F30", {"entities" : qUnion([Q0]), "depth" : 3.5 * mm, "offsetDistance" : 25 * mm});
        }
        {
            var Q0;
            Q0=qCreatedBy(makeId("Front.planeOp"),FACE);
            var sketch = newSketch(context, id + "F31", { "sketchPlane" : qUnion([Q0])});
            skLineSegment(sketch, "E191", {"start": v(31.67, -28.2) * mm, "end": v(31.67, -29.34) * mm});
            skLineSegment(sketch, "E192", {"start": v(31.67, -29.34) * mm, "end": v(41.55, -29.34) * mm});
            skLineSegment(sketch, "E193", {"start": v(41.55, -29.34) * mm, "end": v(41.55, -27.55) * mm});
            skLineSegment(sketch, "E194", {"start": v(41.55, -27.55) * mm, "end": v(35.03, -27.55) * mm});
            skLineSegment(sketch, "E195", {"start": v(31.63, -17.67) * mm, "end": v(32.7, -19.2) * mm});
            skLineSegment(sketch, "E196", {"start": v(31.67, -28.2) * mm, "end": v(36.88, -23.82) * mm});
            skLineSegment(sketch, "E197", {"start": v(35.03, -27.55) * mm, "end": v(38.33, -24.95) * mm});
            skArc(sketch, "E198", {"start": v(41.22, -22.06) * mm, "mid": v(41.06, -18.32) * mm, "end": v(38.05, -16.08) * mm});
            skArc(sketch, "E199", {"start": v(39.1, -21.51) * mm, "mid": v(39.18, -19.3) * mm, "end": v(37.5, -17.84) * mm});
            skArc(sketch, "E200", {"start": v(38.05, -16.08) * mm, "mid": v(34.67, -16.17) * mm, "end": v(31.63, -17.67) * mm});
            skArc(sketch, "E201", {"start": v(38.33, -24.95) * mm, "mid": v(39.86, -23.59) * mm, "end": v(41.22, -22.06) * mm});
            skArc(sketch, "E202", {"start": v(36.88, -23.82) * mm, "mid": v(38.06, -22.72) * mm, "end": v(39.1, -21.51) * mm});
            skArc(sketch, "E203", {"start": v(37.5, -17.84) * mm, "mid": v(34.92, -17.84) * mm, "end": v(32.7, -19.2) * mm});
            skSolve(sketch);
        }
        {
            var Q0;
            Q0=makeQuery(id+"F31.imprint","IMPRINT",FACE,{"disambiguationData":[TD([[makeQuery(id+"F31.imprint","IMPRINT",EDGE,{"derivedFrom":sQuery(id+"F31.wireOp",EDGE,"E191")}),1.0]])]});
            extrude(context, id + "F32", {"entities" : qUnion([Q0]), "depth" : 3.5 * mm, "offsetDistance" : 25 * mm});
        }
        {
            var Q0;
            Q0=makeQuery(id+"F32.opExtrude","SWEPT_EDGE",EDGE,{"disambiguationData":[OSD([sQuery(id+"F31.wireOp",EDGE,"E198"),sQuery(id+"F31.wireOp",EDGE,"E201")])]});
            fillet(context, id + "F33", {"entities" : qUnion([Q0]), "radius" : 4 * mm, "tangentPropagation" : true, "allowEdgeOverflow" : false});
        }
        {
            var Q0;
            Q0=makeQuery(id+"F32.opExtrude","SWEPT_EDGE",EDGE,{"disambiguationData":[OSD([sQuery(id+"F31.wireOp",EDGE,"E199"),sQuery(id+"F31.wireOp",EDGE,"E202")])]});
            fillet(context, id + "F34", {"entities" : qUnion([Q0]), "radius" : 2.12 * mm, "tangentPropagation" : true, "allowEdgeOverflow" : false});
        }
        {
            var Q0;
            Q0=makeQuery(id+"F1.opExtrude","CAP_FACE",FACE,{"disambiguationData":[OSD([sQuery(id+"F0.wireOp",EDGE,"E0"),sQuery(id+"F0.wireOp",EDGE,"E1"),sQuery(id+"F0.wireOp",EDGE,"E2"),sQuery(id+"F0.wireOp",EDGE,"E3"),sQuery(id+"F0.wireOp",EDGE,"E4"),sQuery(id+"F0.wireOp",EDGE,"E5"),sQuery(id+"F0.wireOp",EDGE,"E6"),sQuery(id+"F0.wireOp",EDGE,"E7"),sQuery(id+"F0.wireOp",EDGE,"E8"),sQuery(id+"F0.wireOp",EDGE,"E9"),sQuery(id+"F0.wireOp",EDGE,"E10"),sQuery(id+"F0.wireOp",EDGE,"E11"),sQuery(id+"F0.wireOp",EDGE,"E12"),sQuery(id+"F0.wireOp",EDGE,"E13"),sQuery(id+"F0.wireOp",EDGE,"E14"),sQuery(id+"F0.wireOp",EDGE,"E15"),sQuery(id+"F0.wireOp",EDGE,"E16"),sQuery(id+"F0.wireOp",EDGE,"E17"),sQuery(id+"F0.wireOp",EDGE,"E18"),sQuery(id+"F0.wireOp",EDGE,"E19"),sQuery(id+"F0.wireOp",EDGE,"E20"),sQuery(id+"F0.wireOp",EDGE,"E21")])],"isStart":true});
            var sketch = newSketch(context, id + "F35", { "sketchPlane" : qUnion([Q0])});
            skCircle(sketch, "E204", {"center": v(72.94, 32.74) * mm, "radius": 1 * mm});
            skCircle(sketch, "E205", {"center": v(64.13, 21.7) * mm, "radius": 1 * mm});
            skSolve(sketch);
        }
        {
            var Q0;
            Q0=makeQuery(id+"F35.imprint","IMPRINT",FACE,{"disambiguationData":[TD([[makeQuery(id+"F35.imprint","IMPRINT",EDGE,{"derivedFrom":sQuery(id+"F35.wireOp",EDGE,"E204")}),1.0]])]});
            var Q1;
            Q1=makeQuery(id+"F35.imprint","IMPRINT",FACE,{"disambiguationData":[TD([[makeQuery(id+"F35.imprint","IMPRINT",EDGE,{"derivedFrom":sQuery(id+"F35.wireOp",EDGE,"E205")}),1.0]])]});
            extrude(context, id + "F36", {"entities" : qUnion([Q0, Q1]), "operationType" : NewBodyOperationType.ADD, "depth" : 25 * mm, "offsetDistance" : 25 * mm});
        }
        {
            var Q0;
            Q0=makeQuery(id+"F4.opExtrude","CAP_FACE",FACE,{"disambiguationData":[OSD([sQuery(id+"F3.wireOp",EDGE,"E22"),sQuery(id+"F3.wireOp",EDGE,"E23"),sQuery(id+"F3.wireOp",EDGE,"E24"),sQuery(id+"F3.wireOp",EDGE,"E25"),sQuery(id+"F3.wireOp",EDGE,"E26"),sQuery(id+"F3.wireOp",EDGE,"E27"),sQuery(id+"F3.wireOp",EDGE,"E28"),sQuery(id+"F3.wireOp",EDGE,"E29"),sQuery(id+"F3.wireOp",EDGE,"E30"),sQuery(id+"F3.wireOp",EDGE,"E31"),sQuery(id+"F3.wireOp",EDGE,"E32"),sQuery(id+"F3.wireOp",EDGE,"E33"),sQuery(id+"F3.wireOp",EDGE,"E34"),sQuery(id+"F3.wireOp",EDGE,"E35"),sQuery(id+"F3.wireOp",EDGE,"E36"),sQuery(id+"F3.wireOp",EDGE,"E37"),sQuery(id+"F3.wireOp",EDGE,"E38"),sQuery(id+"F3.wireOp",EDGE,"E39")])],"isStart":true});
            var sketch = newSketch(context, id + "F37", { "sketchPlane" : qUnion([Q0])});
            skCircle(sketch, "E206", {"center": v(50.52, 25) * mm, "radius": 1 * mm});
            skCircle(sketch, "E207", {"center": v(40.08, 25) * mm, "radius": 1 * mm});
            skSolve(sketch);
        }
        {
            var Q0;
            Q0=makeQuery(id+"F37.imprint","IMPRINT",FACE,{"disambiguationData":[TD([[makeQuery(id+"F37.imprint","IMPRINT",EDGE,{"derivedFrom":sQuery(id+"F37.wireOp",EDGE,"E207")}),1.0]])]});
            var Q1;
            Q1=makeQuery(id+"F37.imprint","IMPRINT",FACE,{"disambiguationData":[TD([[makeQuery(id+"F37.imprint","IMPRINT",EDGE,{"derivedFrom":sQuery(id+"F37.wireOp",EDGE,"E206")}),1.0]])]});
            extrude(context, id + "F38", {"entities" : qUnion([Q0, Q1]), "operationType" : NewBodyOperationType.ADD, "depth" : 25 * mm, "offsetDistance" : 25 * mm});
        }
        {
            var Q0;
            Q0=makeQuery(id+"F14.opPattern","COPY",BODY,{"derivedFrom":makeQuery(id+"F4.opExtrude","SWEPT_BODY",BODY,{"disambiguationData":[OSD([sQuery(id+"F3.wireOp",EDGE,"E22"),sQuery(id+"F3.wireOp",EDGE,"E23"),sQuery(id+"F3.wireOp",EDGE,"E24"),sQuery(id+"F3.wireOp",EDGE,"E25"),sQuery(id+"F3.wireOp",EDGE,"E26"),sQuery(id+"F3.wireOp",EDGE,"E27"),sQuery(id+"F3.wireOp",EDGE,"E28"),sQuery(id+"F3.wireOp",EDGE,"E29"),sQuery(id+"F3.wireOp",EDGE,"E30"),sQuery(id+"F3.wireOp",EDGE,"E31"),sQuery(id+"F3.wireOp",EDGE,"E32"),sQuery(id+"F3.wireOp",EDGE,"E33"),sQuery(id+"F3.wireOp",EDGE,"E34"),sQuery(id+"F3.wireOp",EDGE,"E35"),sQuery(id+"F3.wireOp",EDGE,"E36"),sQuery(id+"F3.wireOp",EDGE,"E37"),sQuery(id+"F3.wireOp",EDGE,"E38"),sQuery(id+"F3.wireOp",EDGE,"E39")])]}),"instanceName":"1"});
            deleteBodies(context, id + "F39", {"entities" : qUnion([Q0])});
        }
        {
            var Q0;
            Q0=makeQuery(id+"F4.opExtrude","SWEPT_BODY",BODY,{"disambiguationData":[OSD([sQuery(id+"F3.wireOp",EDGE,"E22"),sQuery(id+"F3.wireOp",EDGE,"E23"),sQuery(id+"F3.wireOp",EDGE,"E24"),sQuery(id+"F3.wireOp",EDGE,"E25"),sQuery(id+"F3.wireOp",EDGE,"E26"),sQuery(id+"F3.wireOp",EDGE,"E27"),sQuery(id+"F3.wireOp",EDGE,"E28"),sQuery(id+"F3.wireOp",EDGE,"E29"),sQuery(id+"F3.wireOp",EDGE,"E30"),sQuery(id+"F3.wireOp",EDGE,"E31"),sQuery(id+"F3.wireOp",EDGE,"E32"),sQuery(id+"F3.wireOp",EDGE,"E33"),sQuery(id+"F3.wireOp",EDGE,"E34"),sQuery(id+"F3.wireOp",EDGE,"E35"),sQuery(id+"F3.wireOp",EDGE,"E36"),sQuery(id+"F3.wireOp",EDGE,"E37"),sQuery(id+"F3.wireOp",EDGE,"E38"),sQuery(id+"F3.wireOp",EDGE,"E39")])]});
            transform(context, id + "F40", {"entities" : qUnion([Q0]), "transformType" : TransformType.TRANSLATION_3D, "dx" : 93.7 * mm, "dy" : 0 * mm, "dz" : 0 * mm, "makeCopy" : true});
        }
        {
            var Q0;
            Q0=makeQuery(id+"F6.opExtrude","CAP_FACE",FACE,{"disambiguationData":[OSD([sQuery(id+"F5.wireOp",EDGE,"E40"),sQuery(id+"F5.wireOp",EDGE,"E41"),sQuery(id+"F5.wireOp",EDGE,"E42"),sQuery(id+"F5.wireOp",EDGE,"E43"),sQuery(id+"F5.wireOp",EDGE,"E44"),sQuery(id+"F5.wireOp",EDGE,"E45"),sQuery(id+"F5.wireOp",EDGE,"E46"),sQuery(id+"F5.wireOp",EDGE,"E47"),sQuery(id+"F5.wireOp",EDGE,"E48"),sQuery(id+"F5.wireOp",EDGE,"E49"),sQuery(id+"F5.wireOp",EDGE,"E50"),sQuery(id+"F5.wireOp",EDGE,"E51"),sQuery(id+"F5.wireOp",EDGE,"E52"),sQuery(id+"F5.wireOp",EDGE,"E53")])],"isStart":true});
            var sketch = newSketch(context, id + "F41", { "sketchPlane" : qUnion([Q0])});
            skCircle(sketch, "E208", {"center": v(27.86, 31.07) * mm, "radius": 1 * mm});
            skCircle(sketch, "E209", {"center": v(27.86, 21.07) * mm, "radius": 1 * mm});
            skSolve(sketch);
        }
        {
            var Q0;
            Q0=makeQuery(id+"F41.imprint","IMPRINT",FACE,{"disambiguationData":[TD([[makeQuery(id+"F41.imprint","IMPRINT",EDGE,{"derivedFrom":sQuery(id+"F41.wireOp",EDGE,"E208")}),1.0]])]});
            var Q1;
            Q1=makeQuery(id+"F41.imprint","IMPRINT",FACE,{"disambiguationData":[TD([[makeQuery(id+"F41.imprint","IMPRINT",EDGE,{"derivedFrom":sQuery(id+"F41.wireOp",EDGE,"E209")}),1.0]])]});
            extrude(context, id + "F42", {"entities" : qUnion([Q0, Q1]), "operationType" : NewBodyOperationType.ADD, "depth" : 25 * mm, "offsetDistance" : 25 * mm});
        }
        {
            var Q0;
            Q0=makeQuery(id+"F8.opExtrude","CAP_FACE",FACE,{"disambiguationData":[OSD([sQuery(id+"F7.wireOp",EDGE,"E54"),sQuery(id+"F7.wireOp",EDGE,"E55"),sQuery(id+"F7.wireOp",EDGE,"E56"),sQuery(id+"F7.wireOp",EDGE,"E57"),sQuery(id+"F7.wireOp",EDGE,"E58"),sQuery(id+"F7.wireOp",EDGE,"E59"),sQuery(id+"F7.wireOp",EDGE,"E60"),sQuery(id+"F7.wireOp",EDGE,"E61"),sQuery(id+"F7.wireOp",EDGE,"E62"),sQuery(id+"F7.wireOp",EDGE,"E63"),sQuery(id+"F7.wireOp",EDGE,"E64"),sQuery(id+"F7.wireOp",EDGE,"E65"),sQuery(id+"F7.wireOp",EDGE,"E66"),sQuery(id+"F7.wireOp",EDGE,"E67"),sQuery(id+"F7.wireOp",EDGE,"E68"),sQuery(id+"F7.wireOp",EDGE,"E69"),sQuery(id+"F7.wireOp",EDGE,"E70"),sQuery(id+"F7.wireOp",EDGE,"E71"),sQuery(id+"F7.wireOp",EDGE,"E72"),sQuery(id+"F7.wireOp",EDGE,"E73"),sQuery(id+"F7.wireOp",EDGE,"E74"),sQuery(id+"F7.wireOp",EDGE,"E75")])],"isStart":true});
            var sketch = newSketch(context, id + "F43", { "sketchPlane" : qUnion([Q0])});
            skCircle(sketch, "E210", {"center": v(11.88, 29.08) * mm, "radius": 1 * mm});
            skCircle(sketch, "E211", {"center": v(1.01, 23.63) * mm, "radius": 1 * mm});
            skSolve(sketch);
        }
        {
            var Q0;
            Q0=makeQuery(id+"F43.imprint","IMPRINT",FACE,{"disambiguationData":[TD([[makeQuery(id+"F43.imprint","IMPRINT",EDGE,{"derivedFrom":sQuery(id+"F43.wireOp",EDGE,"E211")}),1.0]])]});
            var Q1;
            Q1=makeQuery(id+"F43.imprint","IMPRINT",FACE,{"disambiguationData":[TD([[makeQuery(id+"F43.imprint","IMPRINT",EDGE,{"derivedFrom":sQuery(id+"F43.wireOp",EDGE,"E210")}),1.0]])]});
            extrude(context, id + "F44", {"entities" : qUnion([Q0, Q1]), "operationType" : NewBodyOperationType.ADD, "depth" : 25 * mm, "offsetDistance" : 25 * mm});
        }
        {
            var Q0;
            Q0=makeQuery(id+"F15.opPattern","COPY",BODY,{"derivedFrom":makeQuery(id+"F8.opExtrude","SWEPT_BODY",BODY,{"disambiguationData":[OSD([sQuery(id+"F7.wireOp",EDGE,"E54"),sQuery(id+"F7.wireOp",EDGE,"E55"),sQuery(id+"F7.wireOp",EDGE,"E56"),sQuery(id+"F7.wireOp",EDGE,"E57"),sQuery(id+"F7.wireOp",EDGE,"E58"),sQuery(id+"F7.wireOp",EDGE,"E59"),sQuery(id+"F7.wireOp",EDGE,"E60"),sQuery(id+"F7.wireOp",EDGE,"E61"),sQuery(id+"F7.wireOp",EDGE,"E62"),sQuery(id+"F7.wireOp",EDGE,"E63"),sQuery(id+"F7.wireOp",EDGE,"E64"),sQuery(id+"F7.wireOp",EDGE,"E65"),sQuery(id+"F7.wireOp",EDGE,"E66"),sQuery(id+"F7.wireOp",EDGE,"E67"),sQuery(id+"F7.wireOp",EDGE,"E68"),sQuery(id+"F7.wireOp",EDGE,"E69"),sQuery(id+"F7.wireOp",EDGE,"E70"),sQuery(id+"F7.wireOp",EDGE,"E71"),sQuery(id+"F7.wireOp",EDGE,"E72"),sQuery(id+"F7.wireOp",EDGE,"E73"),sQuery(id+"F7.wireOp",EDGE,"E74"),sQuery(id+"F7.wireOp",EDGE,"E75")])]}),"instanceName":"1"});
            deleteBodies(context, id + "F45", {"entities" : qUnion([Q0])});
        }
        {
            var Q0;
            Q0=makeQuery(id+"F8.opExtrude","SWEPT_BODY",BODY,{"disambiguationData":[OSD([sQuery(id+"F7.wireOp",EDGE,"E54"),sQuery(id+"F7.wireOp",EDGE,"E55"),sQuery(id+"F7.wireOp",EDGE,"E56"),sQuery(id+"F7.wireOp",EDGE,"E57"),sQuery(id+"F7.wireOp",EDGE,"E58"),sQuery(id+"F7.wireOp",EDGE,"E59"),sQuery(id+"F7.wireOp",EDGE,"E60"),sQuery(id+"F7.wireOp",EDGE,"E61"),sQuery(id+"F7.wireOp",EDGE,"E62"),sQuery(id+"F7.wireOp",EDGE,"E63"),sQuery(id+"F7.wireOp",EDGE,"E64"),sQuery(id+"F7.wireOp",EDGE,"E65"),sQuery(id+"F7.wireOp",EDGE,"E66"),sQuery(id+"F7.wireOp",EDGE,"E67"),sQuery(id+"F7.wireOp",EDGE,"E68"),sQuery(id+"F7.wireOp",EDGE,"E69"),sQuery(id+"F7.wireOp",EDGE,"E70"),sQuery(id+"F7.wireOp",EDGE,"E71"),sQuery(id+"F7.wireOp",EDGE,"E72"),sQuery(id+"F7.wireOp",EDGE,"E73"),sQuery(id+"F7.wireOp",EDGE,"E74"),sQuery(id+"F7.wireOp",EDGE,"E75")])]});
            transform(context, id + "F46", {"entities" : qUnion([Q0]), "transformType" : TransformType.TRANSLATION_3D, "dx" : 79 * mm, "dy" : 0 * mm, "dz" : 0 * mm, "makeCopy" : true});
        }
        {
            var Q0;
            Q0=makeQuery(id+"F10.opExtrude","CAP_FACE",FACE,{"disambiguationData":[OSD([sQuery(id+"F9.wireOp",EDGE,"E76"),sQuery(id+"F9.wireOp",EDGE,"E77"),sQuery(id+"F9.wireOp",EDGE,"E78"),sQuery(id+"F9.wireOp",EDGE,"E79"),sQuery(id+"F9.wireOp",EDGE,"E80"),sQuery(id+"F9.wireOp",EDGE,"E81"),sQuery(id+"F9.wireOp",EDGE,"E82"),sQuery(id+"F9.wireOp",EDGE,"E83"),sQuery(id+"F9.wireOp",EDGE,"E84"),sQuery(id+"F9.wireOp",EDGE,"E85"),sQuery(id+"F9.wireOp",EDGE,"E86"),sQuery(id+"F9.wireOp",EDGE,"E87"),sQuery(id+"F9.wireOp",EDGE,"E88"),sQuery(id+"F9.wireOp",EDGE,"E89"),sQuery(id+"F9.wireOp",EDGE,"E90"),sQuery(id+"F9.wireOp",EDGE,"E91"),sQuery(id+"F9.wireOp",EDGE,"E92"),sQuery(id+"F9.wireOp",EDGE,"E93"),sQuery(id+"F9.wireOp",EDGE,"E94"),sQuery(id+"F9.wireOp",EDGE,"E95")])],"isStart":true});
            var sketch = newSketch(context, id + "F47", { "sketchPlane" : qUnion([Q0])});
            skCircle(sketch, "E212", {"center": v(-23.07, 32.74) * mm, "radius": 1 * mm});
            skCircle(sketch, "E213", {"center": v(-34.45, 22.2) * mm, "radius": 1 * mm});
            skSolve(sketch);
        }
        {
            var Q0;
            Q0=makeQuery(id+"F47.imprint","IMPRINT",FACE,{"disambiguationData":[TD([[makeQuery(id+"F47.imprint","IMPRINT",EDGE,{"derivedFrom":sQuery(id+"F47.wireOp",EDGE,"E213")}),1.0]])]});
            var Q1;
            Q1=makeQuery(id+"F47.imprint","IMPRINT",FACE,{"disambiguationData":[TD([[makeQuery(id+"F47.imprint","IMPRINT",EDGE,{"derivedFrom":sQuery(id+"F47.wireOp",EDGE,"E212")}),1.0]])]});
            extrude(context, id + "F48", {"entities" : qUnion([Q0, Q1]), "operationType" : NewBodyOperationType.ADD, "depth" : 25 * mm, "offsetDistance" : 25 * mm});
        }
        {
            var Q0;
            Q0=makeQuery(id+"F13.opExtrude","CAP_FACE",FACE,{"disambiguationData":[OSD([sQuery(id+"F12.wireOp",EDGE,"E100"),sQuery(id+"F12.wireOp",EDGE,"E101"),sQuery(id+"F12.wireOp",EDGE,"E102"),sQuery(id+"F12.wireOp",EDGE,"E103"),sQuery(id+"F12.wireOp",EDGE,"E104"),sQuery(id+"F12.wireOp",EDGE,"E105"),sQuery(id+"F12.wireOp",EDGE,"E106"),sQuery(id+"F12.wireOp",EDGE,"E107"),sQuery(id+"F12.wireOp",EDGE,"E108"),sQuery(id+"F12.wireOp",EDGE,"E109"),sQuery(id+"F12.wireOp",EDGE,"E110"),sQuery(id+"F12.wireOp",EDGE,"E111"),sQuery(id+"F12.wireOp",EDGE,"E112"),sQuery(id+"F12.wireOp",EDGE,"E113"),sQuery(id+"F12.wireOp",EDGE,"E114.trimOffspring")])],"isStart":true});
            var sketch = newSketch(context, id + "F49", { "sketchPlane" : qUnion([Q0])});
            skCircle(sketch, "E214", {"center": v(-99.16, 26.96) * mm, "radius": 1 * mm});
            skCircle(sketch, "E215", {"center": v(-88.6, 21.23) * mm, "radius": 1 * mm});
            skPoint(sketch, "E215.centerSnap0", {"position": v(-90.19, 21.23) * mm});
            skSolve(sketch);
        }
        {
            var Q0;
            Q0=makeQuery(id+"F49.imprint","IMPRINT",FACE,{"disambiguationData":[TD([[makeQuery(id+"F49.imprint","IMPRINT",EDGE,{"derivedFrom":sQuery(id+"F49.wireOp",EDGE,"E214")}),1.0]])]});
            var Q1;
            Q1=makeQuery(id+"F49.imprint","IMPRINT",FACE,{"disambiguationData":[TD([[makeQuery(id+"F49.imprint","IMPRINT",EDGE,{"derivedFrom":sQuery(id+"F49.wireOp",EDGE,"E215")}),1.0]])]});
            extrude(context, id + "F50", {"entities" : qUnion([Q0, Q1]), "operationType" : NewBodyOperationType.ADD, "depth" : 25 * mm, "offsetDistance" : 25 * mm});
        }
        {
            var Q0;
            Q0=makeQuery(id+"F13.opExtrude","CAP_FACE",FACE,{"disambiguationData":[OSD([sQuery(id+"F12.wireOp",EDGE,"E96"),sQuery(id+"F12.wireOp",EDGE,"E97"),sQuery(id+"F12.wireOp",EDGE,"E98"),sQuery(id+"F12.wireOp",EDGE,"E99")])],"isStart":true});
            var sketch = newSketch(context, id + "F51", { "sketchPlane" : qUnion([Q0])});
            skCircle(sketch, "E216", {"center": v(-95.2, 38.58) * mm, "radius": 1 * mm});
            skSolve(sketch);
        }
        {
            var Q0;
            Q0=makeQuery(id+"F51.imprint","IMPRINT",FACE,{"disambiguationData":[TD([[makeQuery(id+"F51.imprint","IMPRINT",EDGE,{"derivedFrom":sQuery(id+"F51.wireOp",EDGE,"E216")}),1.0]])]});
            extrude(context, id + "F52", {"entities" : qUnion([Q0]), "operationType" : NewBodyOperationType.ADD, "depth" : 25 * mm, "offsetDistance" : 25 * mm});
        }
        {
            var Q0;
            Q0=makeQuery(id+"F17.opExtrude","CAP_FACE",FACE,{"disambiguationData":[OSD([sQuery(id+"F16.wireOp",EDGE,"E116"),sQuery(id+"F16.wireOp",EDGE,"E117"),sQuery(id+"F16.wireOp",EDGE,"E118"),sQuery(id+"F16.wireOp",EDGE,"E119"),sQuery(id+"F16.wireOp",EDGE,"E120"),sQuery(id+"F16.wireOp",EDGE,"E121"),sQuery(id+"F16.wireOp",EDGE,"E122"),sQuery(id+"F16.wireOp",EDGE,"E123"),sQuery(id+"F16.wireOp",EDGE,"E124"),sQuery(id+"F16.wireOp",EDGE,"E125"),sQuery(id+"F16.wireOp",EDGE,"E126"),sQuery(id+"F16.wireOp",EDGE,"E127")])],"isStart":true});
            var sketch = newSketch(context, id + "F53", { "sketchPlane" : qUnion([Q0])});
            skCircle(sketch, "E217", {"center": v(40.34, -17.7) * mm, "radius": 1 * mm});
            skCircle(sketch, "E218", {"center": v(40.34, -28.15) * mm, "radius": 1 * mm});
            skSolve(sketch);
        }
        {
            var Q0;
            Q0=makeQuery(id+"F53.imprint","IMPRINT",FACE,{"disambiguationData":[TD([[makeQuery(id+"F53.imprint","IMPRINT",EDGE,{"derivedFrom":sQuery(id+"F53.wireOp",EDGE,"E217")}),1.0]])]});
            var Q1;
            Q1=makeQuery(id+"F53.imprint","IMPRINT",FACE,{"disambiguationData":[TD([[makeQuery(id+"F53.imprint","IMPRINT",EDGE,{"derivedFrom":sQuery(id+"F53.wireOp",EDGE,"E218")}),1.0]])]});
            extrude(context, id + "F54", {"entities" : qUnion([Q0, Q1]), "operationType" : NewBodyOperationType.ADD, "depth" : 25 * mm, "offsetDistance" : 25 * mm});
        }
        {
            var Q0;
            Q0=makeQuery(id+"F18.opPattern","COPY",BODY,{"derivedFrom":makeQuery(id+"F17.opExtrude","SWEPT_BODY",BODY,{"disambiguationData":[OSD([sQuery(id+"F16.wireOp",EDGE,"E116"),sQuery(id+"F16.wireOp",EDGE,"E117"),sQuery(id+"F16.wireOp",EDGE,"E118"),sQuery(id+"F16.wireOp",EDGE,"E119"),sQuery(id+"F16.wireOp",EDGE,"E120"),sQuery(id+"F16.wireOp",EDGE,"E121"),sQuery(id+"F16.wireOp",EDGE,"E122"),sQuery(id+"F16.wireOp",EDGE,"E123"),sQuery(id+"F16.wireOp",EDGE,"E124"),sQuery(id+"F16.wireOp",EDGE,"E125"),sQuery(id+"F16.wireOp",EDGE,"E126"),sQuery(id+"F16.wireOp",EDGE,"E127")])]}),"instanceName":"1"});
            deleteBodies(context, id + "F55", {"entities" : qUnion([Q0])});
        }
        {
            var Q0;
            Q0=makeQuery(id+"F17.opExtrude","SWEPT_BODY",BODY,{"disambiguationData":[OSD([sQuery(id+"F16.wireOp",EDGE,"E116"),sQuery(id+"F16.wireOp",EDGE,"E117"),sQuery(id+"F16.wireOp",EDGE,"E118"),sQuery(id+"F16.wireOp",EDGE,"E119"),sQuery(id+"F16.wireOp",EDGE,"E120"),sQuery(id+"F16.wireOp",EDGE,"E121"),sQuery(id+"F16.wireOp",EDGE,"E122"),sQuery(id+"F16.wireOp",EDGE,"E123"),sQuery(id+"F16.wireOp",EDGE,"E124"),sQuery(id+"F16.wireOp",EDGE,"E125"),sQuery(id+"F16.wireOp",EDGE,"E126"),sQuery(id+"F16.wireOp",EDGE,"E127")])]});
            transform(context, id + "F56", {"entities" : qUnion([Q0]), "transformType" : TransformType.TRANSLATION_3D, "dx" : 103.4 * mm, "dy" : 0 * mm, "dz" : 0 * mm, "makeCopy" : true});
        }
        {
            var Q0;
            Q0=makeQuery(id+"F26.opExtrude","CAP_FACE",FACE,{"disambiguationData":[OSD([sQuery(id+"F25.wireOp",EDGE,"E154"),sQuery(id+"F25.wireOp",EDGE,"E155"),sQuery(id+"F25.wireOp",EDGE,"E156"),sQuery(id+"F25.wireOp",EDGE,"E157"),sQuery(id+"F25.wireOp",EDGE,"E158"),sQuery(id+"F25.wireOp",EDGE,"E159"),sQuery(id+"F25.wireOp",EDGE,"E160"),sQuery(id+"F25.wireOp",EDGE,"E161"),sQuery(id+"F25.wireOp",EDGE,"E162"),sQuery(id+"F25.wireOp",EDGE,"E163"),sQuery(id+"F25.wireOp",EDGE,"E164"),sQuery(id+"F25.wireOp",EDGE,"E167"),sQuery(id+"F25.wireOp",EDGE,"E168"),sQuery(id+"F25.wireOp",EDGE,"E169"),sQuery(id+"F25.wireOp",EDGE,"E170"),sQuery(id+"F25.wireOp",EDGE,"E171.trimOffspring")])],"isStart":true});
            var sketch = newSketch(context, id + "F57", { "sketchPlane" : qUnion([Q0])});
            skCircle(sketch, "E219", {"center": v(32.84, -22.6) * mm, "radius": 1 * mm});
            skPoint(sketch, "E219.centerSnap0", {"position": v(34.09, -22.6) * mm});
            skCircle(sketch, "E220", {"center": v(23.43, -23.05) * mm, "radius": 1 * mm});
            skSolve(sketch);
        }
        {
            var Q0;
            Q0=makeQuery(id+"F57.imprint","IMPRINT",FACE,{"disambiguationData":[TD([[makeQuery(id+"F57.imprint","IMPRINT",EDGE,{"derivedFrom":sQuery(id+"F57.wireOp",EDGE,"E220")}),1.0]])]});
            var Q1;
            Q1=makeQuery(id+"F57.imprint","IMPRINT",FACE,{"disambiguationData":[TD([[makeQuery(id+"F57.imprint","IMPRINT",EDGE,{"derivedFrom":sQuery(id+"F57.wireOp",EDGE,"E219")}),1.0]])]});
            extrude(context, id + "F58", {"entities" : qUnion([Q0, Q1]), "operationType" : NewBodyOperationType.ADD, "depth" : 25 * mm, "offsetDistance" : 25 * mm});
        }
        {
            var Q0;
            Q0=makeQuery(id+"F28.opExtrude","CAP_FACE",FACE,{"disambiguationData":[OSD([sQuery(id+"F27.wireOp",EDGE,"E173"),sQuery(id+"F27.wireOp",EDGE,"E174"),sQuery(id+"F27.wireOp",EDGE,"E175"),sQuery(id+"F27.wireOp",EDGE,"E176"),sQuery(id+"F27.wireOp",EDGE,"E177"),sQuery(id+"F27.wireOp",EDGE,"E178"),sQuery(id+"F27.wireOp",EDGE,"E179"),sQuery(id+"F27.wireOp",EDGE,"E180"),sQuery(id+"F27.wireOp",EDGE,"E181"),sQuery(id+"F27.wireOp",EDGE,"E182"),sQuery(id+"F27.wireOp",EDGE,"E183"),sQuery(id+"F27.wireOp",EDGE,"E184"),sQuery(id+"F27.wireOp",EDGE,"E185"),sQuery(id+"F27.wireOp",EDGE,"E186"),sQuery(id+"F27.wireOp",EDGE,"E187"),sQuery(id+"F27.wireOp",EDGE,"E188"),sQuery(id+"F27.wireOp",EDGE,"E189")])],"isStart":true});
            var sketch = newSketch(context, id + "F59", { "sketchPlane" : qUnion([Q0])});
            skCircle(sketch, "E221", {"center": v(11.36, -19.12) * mm, "radius": 1 * mm});
            skPoint(sketch, "E221.centerSnap0", {"position": v(10.12, -19.12) * mm});
            skCircle(sketch, "E222", {"center": v(10.5, -30.06) * mm, "radius": 1 * mm});
            skSolve(sketch);
        }
        {
            var Q0;
            Q0=makeQuery(id+"F59.imprint","IMPRINT",FACE,{"disambiguationData":[TD([[makeQuery(id+"F59.imprint","IMPRINT",EDGE,{"derivedFrom":sQuery(id+"F59.wireOp",EDGE,"E221")}),1.0]])]});
            var Q1;
            Q1=makeQuery(id+"F59.imprint","IMPRINT",FACE,{"disambiguationData":[TD([[makeQuery(id+"F59.imprint","IMPRINT",EDGE,{"derivedFrom":sQuery(id+"F59.wireOp",EDGE,"E222")}),1.0]])]});
            extrude(context, id + "F60", {"entities" : qUnion([Q0, Q1]), "operationType" : NewBodyOperationType.ADD, "depth" : 25 * mm, "offsetDistance" : 25 * mm});
        }
        {
            var Q0;
            Q0=makeQuery(id+"F20.opExtrude","CAP_FACE",FACE,{"disambiguationData":[OSD([sQuery(id+"F19.wireOp",EDGE,"E128"),sQuery(id+"F19.wireOp",EDGE,"E129"),sQuery(id+"F19.wireOp",EDGE,"E130"),sQuery(id+"F19.wireOp",EDGE,"E131"),sQuery(id+"F19.wireOp",EDGE,"E132"),sQuery(id+"F19.wireOp",EDGE,"E133"),sQuery(id+"F19.wireOp",EDGE,"E134"),sQuery(id+"F19.wireOp",EDGE,"E135"),sQuery(id+"F19.wireOp",EDGE,"E136"),sQuery(id+"F19.wireOp",EDGE,"E137"),sQuery(id+"F19.wireOp",EDGE,"E138.trimOffspring"),sQuery(id+"F19.wireOp",EDGE,"E139.trimOffspring"),sQuery(id+"F19.wireOp",EDGE,"E140.trimOffspring"),sQuery(id+"F19.wireOp",EDGE,"E141.trimOffspring")])],"isStart":true});
            var sketch = newSketch(context, id + "F61", { "sketchPlane" : qUnion([Q0])});
            skCircle(sketch, "E223", {"center": v(-2.6, -17.5) * mm, "radius": 1 * mm});
            skCircle(sketch, "E224", {"center": v(-2.85, -28.58) * mm, "radius": 1 * mm});
            skSolve(sketch);
        }
        {
            var Q0;
            Q0=makeQuery(id+"F61.imprint","IMPRINT",FACE,{"disambiguationData":[TD([[makeQuery(id+"F61.imprint","IMPRINT",EDGE,{"derivedFrom":sQuery(id+"F61.wireOp",EDGE,"E223")}),1.0]])]});
            var Q1;
            Q1=makeQuery(id+"F61.imprint","IMPRINT",FACE,{"disambiguationData":[TD([[makeQuery(id+"F61.imprint","IMPRINT",EDGE,{"derivedFrom":sQuery(id+"F61.wireOp",EDGE,"E224")}),1.0]])]});
            extrude(context, id + "F62", {"entities" : qUnion([Q0, Q1]), "operationType" : NewBodyOperationType.ADD, "depth" : 25 * mm, "offsetDistance" : 25 * mm});
        }
        {
            var Q0;
            Q0=makeQuery(id+"F30.opExtrude","CAP_FACE",FACE,{"disambiguationData":[OSD([sQuery(id+"F29.wireOp",EDGE,"E190.bottom"),sQuery(id+"F29.wireOp",EDGE,"E190.top"),sQuery(id+"F29.wireOp",EDGE,"E190.left"),sQuery(id+"F29.wireOp",EDGE,"E190.right")])],"isStart":true});
            var sketch = newSketch(context, id + "F63", { "sketchPlane" : qUnion([Q0])});
            skCircle(sketch, "E225", {"center": v(-20.47, -22.28) * mm, "radius": 1 * mm});
            skCircle(sketch, "E226", {"center": v(-15.86, -22.28) * mm, "radius": 1 * mm});
            skSolve(sketch);
        }
        {
            var Q0;
            Q0=makeQuery(id+"F63.imprint","IMPRINT",FACE,{"disambiguationData":[TD([[makeQuery(id+"F63.imprint","IMPRINT",EDGE,{"derivedFrom":sQuery(id+"F63.wireOp",EDGE,"E225")}),1.0]])]});
            var Q1;
            Q1=makeQuery(id+"F63.imprint","IMPRINT",FACE,{"disambiguationData":[TD([[makeQuery(id+"F63.imprint","IMPRINT",EDGE,{"derivedFrom":sQuery(id+"F63.wireOp",EDGE,"E226")}),1.0]])]});
            extrude(context, id + "F64", {"entities" : qUnion([Q0, Q1]), "operationType" : NewBodyOperationType.ADD, "depth" : 25 * mm, "offsetDistance" : 25 * mm});
        }
        {
            var Q0;
            Q0=makeQuery(id+"F32.opExtrude","CAP_FACE",FACE,{"disambiguationData":[OSD([sQuery(id+"F31.wireOp",EDGE,"E191"),sQuery(id+"F31.wireOp",EDGE,"E192"),sQuery(id+"F31.wireOp",EDGE,"E193"),sQuery(id+"F31.wireOp",EDGE,"E194"),sQuery(id+"F31.wireOp",EDGE,"E195"),sQuery(id+"F31.wireOp",EDGE,"E196"),sQuery(id+"F31.wireOp",EDGE,"E197"),sQuery(id+"F31.wireOp",EDGE,"E198"),sQuery(id+"F31.wireOp",EDGE,"E199"),sQuery(id+"F31.wireOp",EDGE,"E200"),sQuery(id+"F31.wireOp",EDGE,"E201"),sQuery(id+"F31.wireOp",EDGE,"E202"),sQuery(id+"F31.wireOp",EDGE,"E203")])],"isStart":true});
            var sketch = newSketch(context, id + "F65", { "sketchPlane" : qUnion([Q0])});
            skCircle(sketch, "E227", {"center": v(-40.1, -18.9) * mm, "radius": 1 * mm});
            skCircle(sketch, "E228", {"center": v(-33.77, -28.2) * mm, "radius": 1 * mm});
            skSolve(sketch);
        }
        {
            var Q0;
            Q0=makeQuery(id+"F65.imprint","IMPRINT",FACE,{"disambiguationData":[TD([[makeQuery(id+"F65.imprint","IMPRINT",EDGE,{"derivedFrom":sQuery(id+"F65.wireOp",EDGE,"E228")}),1.0]])]});
            var Q1;
            Q1=makeQuery(id+"F65.imprint","IMPRINT",FACE,{"disambiguationData":[TD([[makeQuery(id+"F65.imprint","IMPRINT",EDGE,{"derivedFrom":sQuery(id+"F65.wireOp",EDGE,"E227")}),1.0]])]});
            extrude(context, id + "F66", {"entities" : qUnion([Q0, Q1]), "operationType" : NewBodyOperationType.ADD, "depth" : 25 * mm, "offsetDistance" : 25 * mm});
        }
        {
            var Q0;
            Q0=makeQuery(id+"F24.opExtrude","CAP_FACE",FACE,{"disambiguationData":[OSD([sQuery(id+"F23.wireOp",EDGE,"E149"),sQuery(id+"F23.wireOp",EDGE,"E150"),sQuery(id+"F23.wireOp",EDGE,"E151"),sQuery(id+"F23.wireOp",EDGE,"E152"),sQuery(id+"F23.wireOp",EDGE,"E153")])],"isStart":true});
            var sketch = newSketch(context, id + "F67", { "sketchPlane" : qUnion([Q0])});
            skCircle(sketch, "E229", {"center": v(-56.82, -22.75) * mm, "radius": 1 * mm});
            skCircle(sketch, "E230", {"center": v(-45.3, -22.75) * mm, "radius": 1 * mm});
            skPoint(sketch, "E230.centerSnap0", {"position": v(-46.43, -22.75) * mm});
            skSolve(sketch);
        }
        {
            var Q0;
            Q0=makeQuery(id+"F67.imprint","IMPRINT",FACE,{"disambiguationData":[TD([[makeQuery(id+"F67.imprint","IMPRINT",EDGE,{"derivedFrom":sQuery(id+"F67.wireOp",EDGE,"E229")}),1.0]])]});
            var Q1;
            Q1=makeQuery(id+"F67.imprint","IMPRINT",FACE,{"disambiguationData":[TD([[makeQuery(id+"F67.imprint","IMPRINT",EDGE,{"derivedFrom":sQuery(id+"F67.wireOp",EDGE,"E230")}),1.0]])]});
            extrude(context, id + "F68", {"entities" : qUnion([Q0, Q1]), "operationType" : NewBodyOperationType.ADD, "depth" : 25 * mm, "offsetDistance" : 25 * mm});
        }
        {
            var Q0;
            Q0=makeQuery(id+"F22.opExtrude","CAP_FACE",FACE,{"disambiguationData":[OSD([sQuery(id+"F21.wireOp",EDGE,"E142"),sQuery(id+"F21.wireOp",EDGE,"E143"),sQuery(id+"F21.wireOp",EDGE,"E144"),sQuery(id+"F21.wireOp",EDGE,"E145"),sQuery(id+"F21.wireOp",EDGE,"E146"),sQuery(id+"F21.wireOp",EDGE,"E147"),sQuery(id+"F21.wireOp",EDGE,"E148")])],"isStart":true});
            var sketch = newSketch(context, id + "F69", { "sketchPlane" : qUnion([Q0])});
            skCircle(sketch, "E231", {"center": v(-78.12, -17.6) * mm, "radius": 1 * mm});
            skCircle(sketch, "E232", {"center": v(-72.45, -31.7) * mm, "radius": 1 * mm});
            skSolve(sketch);
        }
        {
            var Q0;
            Q0=makeQuery(id+"F69.imprint","IMPRINT",FACE,{"disambiguationData":[TD([[makeQuery(id+"F69.imprint","IMPRINT",EDGE,{"derivedFrom":sQuery(id+"F69.wireOp",EDGE,"E231")}),1.0]])]});
            var Q1;
            {var subQ0=sQuery(id+"F69.wireOp",EDGE,"E232");var subQ1=makeQuery(id+"F22.opExtrude","CAP_EDGE",EDGE,{"disambiguationData":[OSD([sQuery(id+"F21.wireOp",EDGE,"E148")])],"isStart":true});var subQ2=makeQuery(id+"F69.imprint","INTERSECT",VERTEX,{"disambiguationData":[OD(0.0)],"derivedFrom":[subQ1,subQ0]});Q1=makeQuery(id+"F69.imprint","IMPRINT",FACE,{"disambiguationData":[TD([[makeQuery(id+"F69.imprint","IMPRINT",EDGE,{"disambiguationData":[TD([[subQ2,1.0]])],"derivedFrom":subQ0}),1.0]])]});}
            extrude(context, id + "F70", {"entities" : qUnion([Q0, Q1]), "operationType" : NewBodyOperationType.ADD, "depth" : 25 * mm, "offsetDistance" : 25 * mm});
        }
    });
